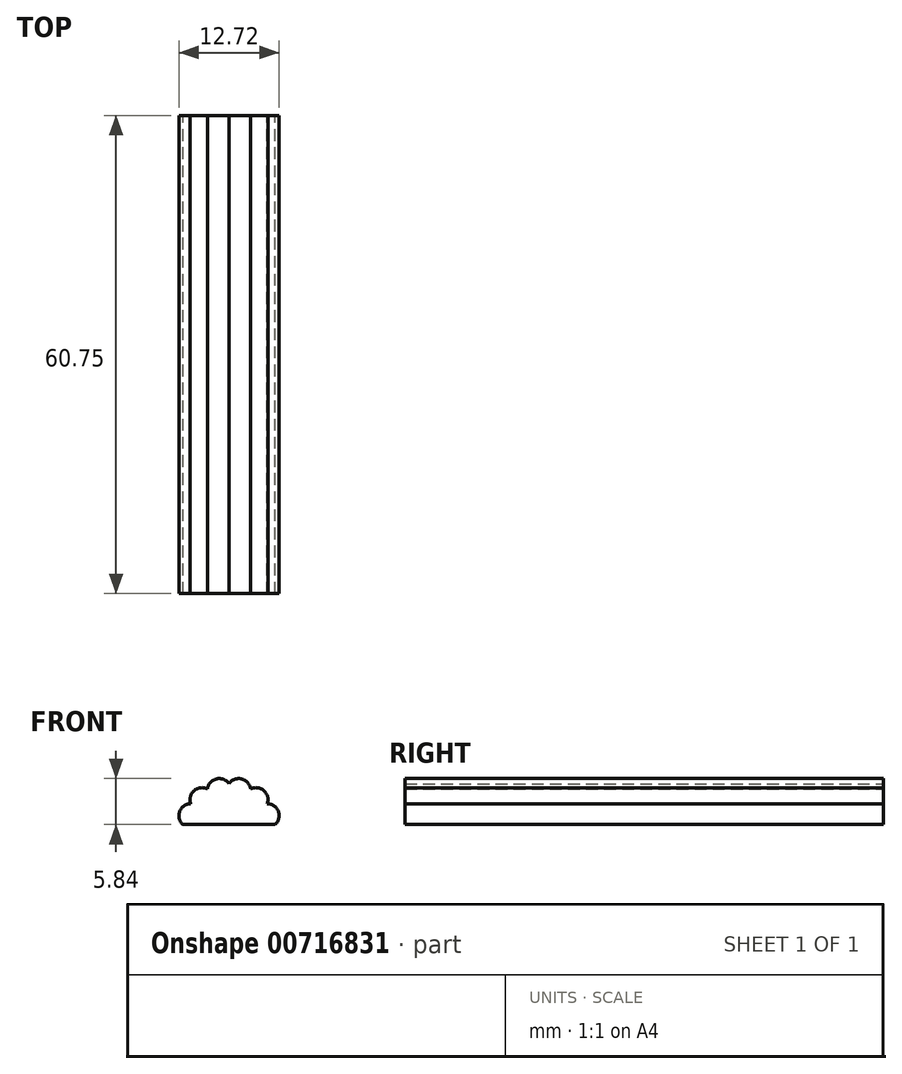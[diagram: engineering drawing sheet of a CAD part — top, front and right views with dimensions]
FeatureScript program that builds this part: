
annotation { "Feature Type Name" : "Feature", "Feature Type Description" : "" }
export const myFeature = defineFeature(function(context is Context, id is Id, definition is map)
    precondition{}
    {
        {
            var Q0;
            Q0=qCreatedBy(makeId("Front.planeOp"),FACE);
            var sketch = newSketch(context, id + "F0", { "sketchPlane" : qUnion([Q0])});
            skArc(sketch, "E0", {"start": v(2.74, 4.51) * mm, "mid": v(1.6, 5.8) * mm, "end": v(0, 5.19) * mm});
            skArc(sketch, "E1.1.0", {"start": v(0, 5.19) * mm, "mid": v(-1.6, 5.8) * mm, "end": v(-2.74, 4.51) * mm});
            skArc(sketch, "E1.2.0", {"start": v(-2.74, 4.51) * mm, "mid": v(-4.44, 4.3) * mm, "end": v(-4.86, 2.64) * mm});
            skArc(sketch, "E1.3.0", {"start": v(-4.86, 2.64) * mm, "mid": v(-6.26, 1.66) * mm, "end": v(-5.86, 0) * mm});
            skArc(sketch, "E1.4.0", {"start": v(-5.86, 0) * mm, "mid": v(-6.65, -1.52) * mm, "end": v(-5.52, -2.8) * mm});
            skArc(sketch, "E1.5.0", {"start": v(-5.52, -2.8) * mm, "mid": v(-5.51, -4.52) * mm, "end": v(-3.91, -5.13) * mm});
            skArc(sketch, "E1.6.0", {"start": v(-3.91, -5.13) * mm, "mid": v(-3.11, -6.64) * mm, "end": v(-1.41, -6.44) * mm});
            skArc(sketch, "E1.7.0", {"start": v(-1.41, -6.44) * mm, "mid": v(0, -7.41) * mm, "end": v(1.41, -6.44) * mm});
            skArc(sketch, "E1.8.0", {"start": v(1.41, -6.44) * mm, "mid": v(3.11, -6.64) * mm, "end": v(3.91, -5.13) * mm});
            skArc(sketch, "E1.9.0", {"start": v(3.91, -5.13) * mm, "mid": v(5.51, -4.52) * mm, "end": v(5.52, -2.8) * mm});
            skArc(sketch, "E1.10.0", {"start": v(5.52, -2.8) * mm, "mid": v(6.65, -1.52) * mm, "end": v(5.86, 0) * mm});
            skArc(sketch, "E1.11.0", {"start": v(5.86, 0) * mm, "mid": v(6.26, 1.66) * mm, "end": v(4.86, 2.64) * mm});
            skArc(sketch, "E1.12.0", {"start": v(4.86, 2.64) * mm, "mid": v(4.44, 4.3) * mm, "end": v(2.74, 4.51) * mm});
            skPoint(sketch, "E1.center", {"position": v(0, -0.71) * mm});
            skPoint(sketch, "E2", {"position": v(1.6, 5.8) * mm});
            skSolve(sketch);
        }
        {
            var Q0;
            Q0 = qSketchRegion(id + "F0", true);
            extrude(context, id + "F1", {"entities" : qUnion([Q0]), "depth" : 60.75 * mm, "offsetDistance" : 25 * mm});
        }
        {
            var Q0;
            Q0=qCreatedBy(makeId("Front.planeOp"),FACE);
            var sketch = newSketch(context, id + "F2", { "sketchPlane" : qUnion([Q0])});
            skLineSegment(sketch, "E3.bottom", {"start": v(-15.24, 0) * mm, "end": v(14.73, 0) * mm});
            skLineSegment(sketch, "E3.top", {"start": v(-15.24, -12.15) * mm, "end": v(14.73, -12.15) * mm});
            skLineSegment(sketch, "E3.left", {"start": v(-15.24, 0) * mm, "end": v(-15.24, -12.15) * mm});
            skLineSegment(sketch, "E3.right", {"start": v(14.73, 0) * mm, "end": v(14.73, -12.15) * mm});
            skSolve(sketch);
        }
        {
            var Q0;
            Q0 = qSketchRegion(id + "F2", true);
            extrude(context, id + "F3", {"entities" : qUnion([Q0]), "operationType" : NewBodyOperationType.REMOVE, "depth" : 80 * mm, "offsetDistance" : 25 * mm});
        }
    });
